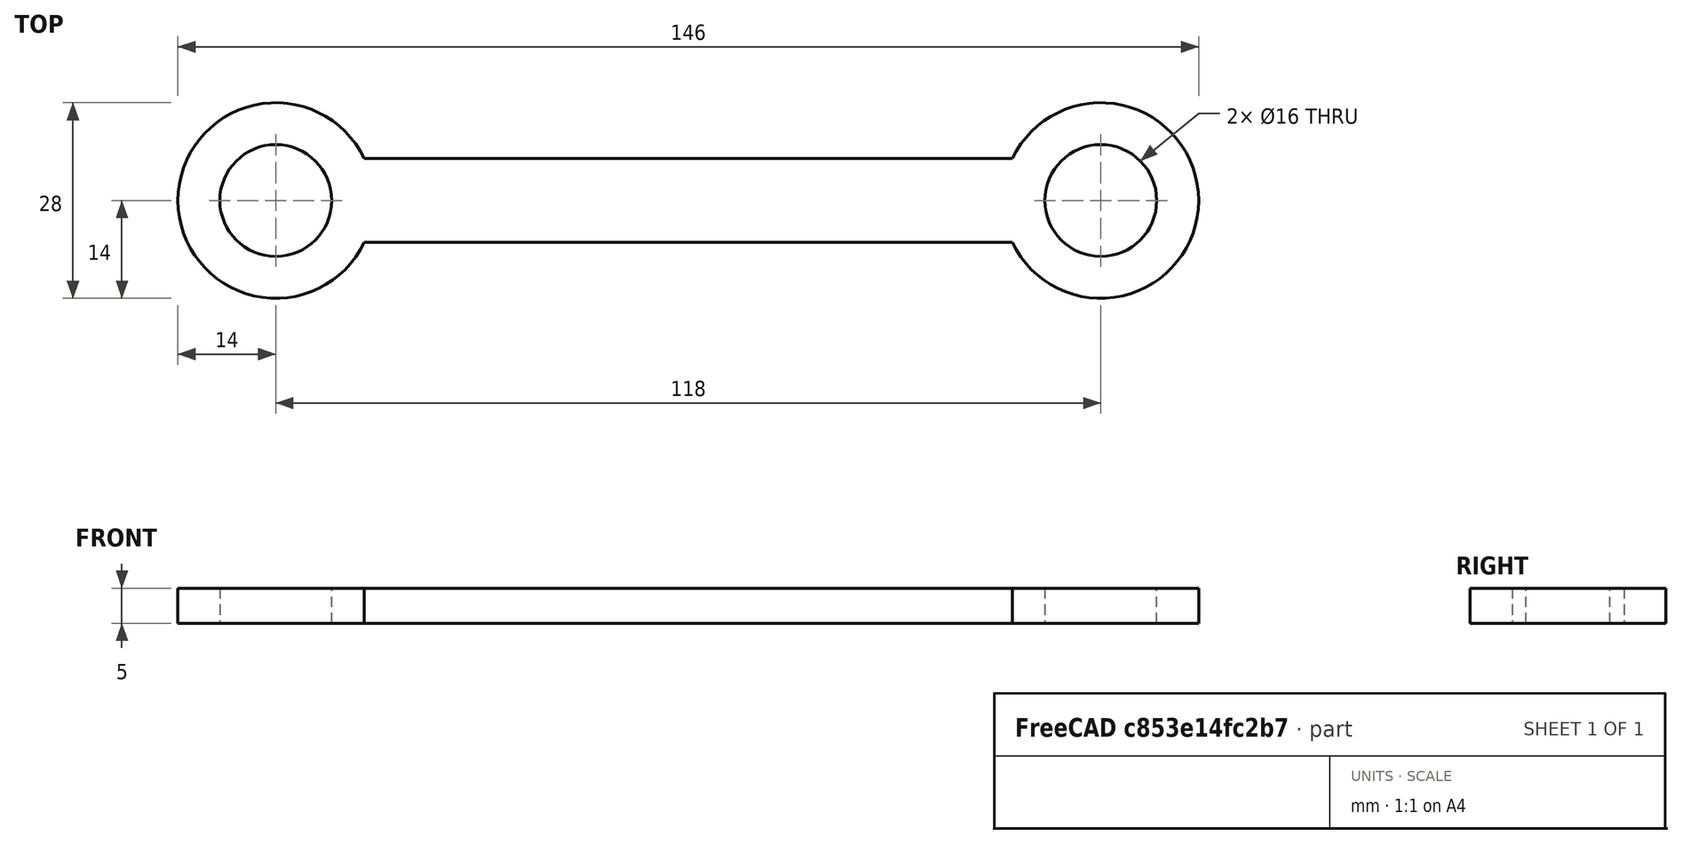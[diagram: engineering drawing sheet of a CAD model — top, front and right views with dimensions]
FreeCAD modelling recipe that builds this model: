
FCSTD DOCUMENT  (FreeCAD 0.19R24276 (Git))
Label: Knife_holder_v3_L118
License: All rights reserved
LicenseURL: http://en.wikipedia.org/wiki/All_rights_reserved
objects: Sketcher::SketchObject×2, PartDesign::Pad×1, PartDesign::Body×1
note: 5 computed .brp shape members not serialized (recipe doc carries the construction recipe); baked Part::Feature solids carry a one-line shape summary decoded from their .brp

FEATURE [Sketcher::SketchObject] Sketch
  FullyConstrained = false
  MapMode = 5
  Support = -> [XY_Plane]
  sketch-geometry (7):
    g0: Circle CenterX=0 CenterY=0 CenterZ=0 NormalX=0 NormalY=0 NormalZ=1 AngleXU=0 Radius=8
    g1: ArcOfCircle CenterX=0 CenterY=0 CenterZ=0 NormalX=0 NormalY=0 NormalZ=1 AngleXU=0 Radius=14 StartAngle=3.58436 EndAngle=8.98172
    g2: Circle CenterX=-118 CenterY=0 CenterZ=0 NormalX=0 NormalY=0 NormalZ=1 AngleXU=0 Radius=8
    g3: ArcOfCircle CenterX=-118 CenterY=0 CenterZ=0 NormalX=0 NormalY=0 NormalZ=1 AngleXU=0 Radius=14 StartAngle=0.443056 EndAngle=5.84042
    g4: LineSegment StartX=-105.352 StartY=6.00183 StartZ=0 EndX=-12.6482 EndY=6.00183 EndZ=0
    g5: LineSegment StartX=-12.65 StartY=-5.99817 StartZ=0 EndX=-105.35 EndY=-5.99817 EndZ=0
    g6: LineSegment StartX=0 StartY=0 StartZ=0 EndX=-59 EndY=0 EndZ=0
  constraints (19):
    c: Coincident(g0,g-1)
    c: Diameter(g0) = 16
    c: Coincident(g1,g0)
    c: Diameter(g1) = 28
    c: PointOnObject(g2,g-1)
    c: Equal(g0,g2)
    c: Coincident(g3,g2)
    c: Equal(g3,g1)
    c: DistanceX(g2,g0) = 118
    c: Horizontal(g4)
    c: Horizontal(g5)
    c: Coincident(g6,g0)
    c: PointOnObject(g6,g-1)
    c: DistanceX(g6,g6) = 59
    c: DistanceY(g5,g4) = 12
    c: Coincident(g3,g4)
    c: Coincident(g3,g5)
    c: Coincident(g1,g4)
    c: Coincident(g1,g5)
FEATURE [PartDesign::Pad] Pad
  Direction = (1,1,1)
  Length = 5
  Length2 = 100
  Profile = -> Sketch
  Type = 0
FEATURE [Sketcher::SketchObject] Sketch001
  FullyConstrained = true
  MapMode = 5
  Placement = pos=(0,0,5) rot=(0,0,1;0rad)
  Support = -> [Pad]
FEATURE [PartDesign::Body] Body
  Group = -> [Sketch,Pad,Sketch001]
  Origin = -> Origin
  Tip = -> Pad
